# Revit family: 6209_Eisenrohranschluß mit Konus
name_source: partatom
category: Rohrformteile
units: mm (PartAtom-declared; Revit-internal decimal feet)

## family parameters
Arbeitsebenenbasiert = Nein
Beim Laden mit Abzugskörper schneiden = Nein
Bemaßung runder Anschluss = Durchmesser verwenden
Gemeinsam genutzt = Nein
Immer vertikal = Ja
OmniClass-Nummer = 23.65.55.14
OmniClass-Titel = Valves for Liquid Services
Teiletyp = Verbindung

## types (2) — shared parameters
Anschlussstück = Messing CW614N, vernickelt
Ausführung = Eisenrohranschluss mit Konus 90°, Mutter und Anschlussstück.
Hersteller = HERZ Armaturen Ges.m.b.H.
Hinweiß = Der O-Ring dient als zusätzliche Dichtung, bei Verlust ist der Eisenrohranschluss metallisch dichtend.
Max. Betriebsdruck = 1000000.0 Pa
Max. Betriebstemperatur = 110 °C
Medium = Heizungswasser nach ÖNORM H5195 oder VDI- Richtlinie 2035.
Die Verwendung von Ethylen- oder Propyleneglykol in einem Mischungsverhältnis 25- 50% ist zulässig.
Mutter = Messing CW614N, vernickelt
O-Ring = EPDM
S02 = 8 mm  [stored 0.0262467 ft]
SCRNCODE = 07;01;02
SCRNSEQ = AWI;AWI_TYP="1001";2
URL = www.herz-armaturen.at
zero-valued in all types: Vorgabe-Ansicht

## per-type parameters (varying)
| type | 5_4x1 | 7_4x5_4 |
| G1 1/4 x R1 | Ja | Nein |
| G1 3/4 x R1 1/4 | Nein | Ja |

note: [stored X ft] marks values corroborated as IEEE doubles in the binary element streams (Revit-internal decimal feet)
